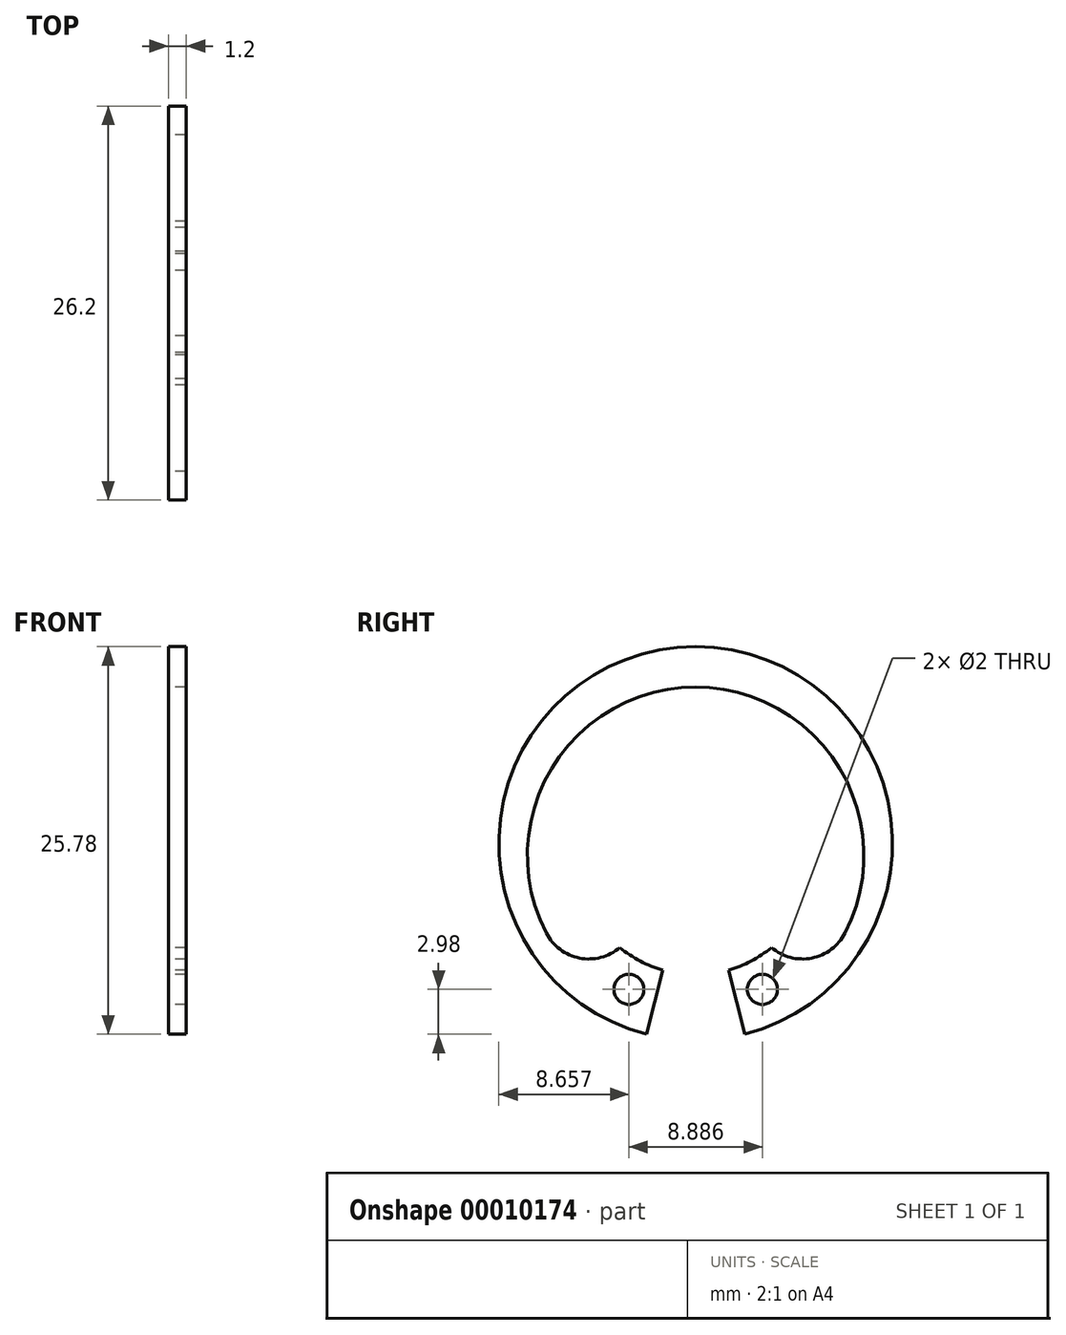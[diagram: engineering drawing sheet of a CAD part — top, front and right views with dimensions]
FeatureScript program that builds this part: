
annotation { "Feature Type Name" : "Feature", "Feature Type Description" : "" }
export const myFeature = defineFeature(function(context is Context, id is Id, definition is map)
    precondition{}
    {
        {
            var Q0;
            Q0=qCreatedBy(makeId("Right.planeOp"),FACE);
            var sketch = newSketch(context, id + "F0", { "sketchPlane" : qUnion([Q0])});
            skArc(sketch, "E0", {"start": v(3.28, -12.68) * mm, "mid": v(0, 13.1) * mm, "end": v(-3.28, -12.68) * mm});
            skArc(sketch, "E1", {"start": v(9.94, -5.95) * mm, "mid": v(0, 10.4) * mm, "end": v(-9.94, -5.95) * mm});
            skLineSegment(sketch, "E2", {"start": v(-2.18, -8.42) * mm, "end": v(-3.28, -12.68) * mm});
            skLineSegment(sketch, "E3", {"start": v(0, 0) * mm, "end": v(0, -15.26) * mm, "construction": true});
            skLineSegment(sketch, "E4", {"start": v(2.18, -8.42) * mm, "end": v(3.28, -12.68) * mm});
            skArc(sketch, "E5", {"start": v(2.18, -8.42) * mm, "mid": v(3.69, -7.82) * mm, "end": v(5.04, -6.92) * mm});
            skLineSegment(sketch, "E6", {"start": v(5.04, -3.36) * mm, "end": v(5.04, -6.92) * mm, "construction": true});
            skLineSegment(sketch, "E7", {"start": v(-5.04, -3.6) * mm, "end": v(-5.04, -6.92) * mm, "construction": true});
            skArc(sketch, "E8", {"start": v(-9.94, -5.95) * mm, "mid": v(-7.73, -7.62) * mm, "end": v(-5.04, -6.92) * mm});
            skArc(sketch, "E9.trimOffspring", {"start": v(-5.04, -6.92) * mm, "mid": v(-3.69, -7.82) * mm, "end": v(-2.18, -8.42) * mm});
            skArc(sketch, "E10", {"start": v(5.04, -6.92) * mm, "mid": v(7.73, -7.62) * mm, "end": v(9.94, -5.95) * mm});
            skCircle(sketch, "E11", {"center": v(4.44, -9.7) * mm, "radius": 1 * mm});
            skCircle(sketch, "E12", {"center": v(-4.44, -9.7) * mm, "radius": 1 * mm});
            skSolve(sketch);
        }
        {
            var Q0;
            Q0=makeQuery(id+"F0.imprint","IMPRINT",FACE,{"disambiguationData":[TD([[makeQuery(id+"F0.imprint","IMPRINT",EDGE,{"derivedFrom":sQuery(id+"F0.wireOp",EDGE,"E0")}),1.0]])]});
            extrude(context, id + "F1", {"entities" : qUnion([Q0]), "depth" : 1.2 * mm});
        }
    });
